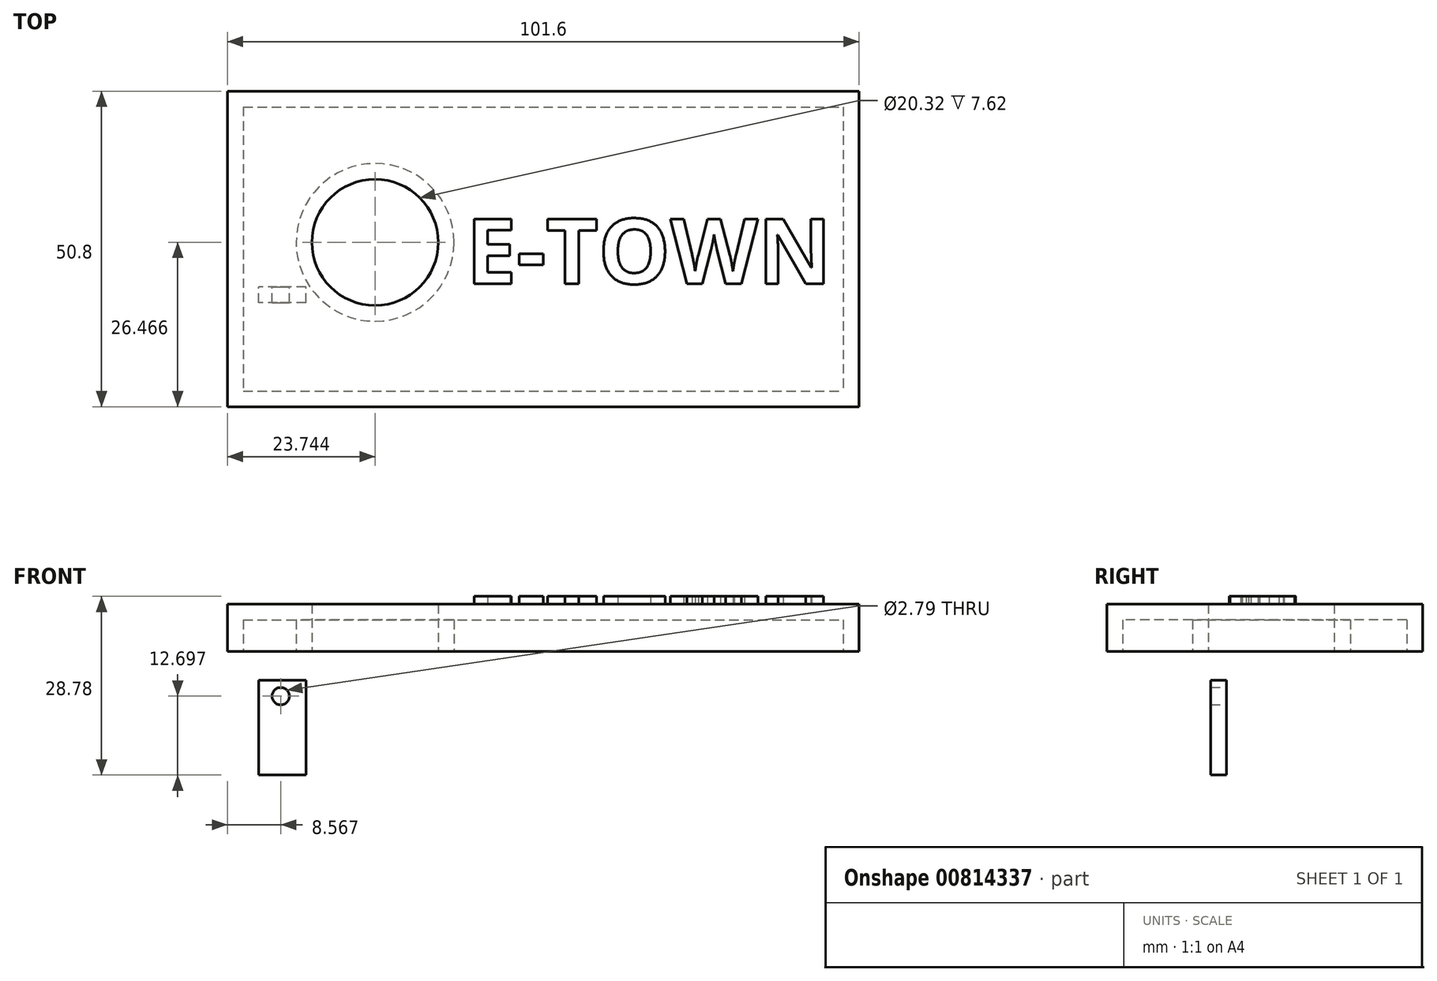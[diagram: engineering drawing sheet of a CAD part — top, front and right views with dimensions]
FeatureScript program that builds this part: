
annotation { "Feature Type Name" : "Feature", "Feature Type Description" : "" }
export const myFeature = defineFeature(function(context is Context, id is Id, definition is map)
    precondition{}
    {
        {
            var Q0;
            Q0=qCreatedBy(makeId("Top.planeOp"),FACE);
            var sketch = newSketch(context, id + "F0", { "sketchPlane" : qUnion([Q0])});
            skLineSegment(sketch, "E0.bottom", {"start": v(-46.2, 31.5) * mm, "end": v(55.4, 31.5) * mm});
            skLineSegment(sketch, "E0.top", {"start": v(-46.2, -19.3) * mm, "end": v(55.4, -19.3) * mm});
            skLineSegment(sketch, "E0.left", {"start": v(-46.2, 31.5) * mm, "end": v(-46.2, -19.3) * mm});
            skLineSegment(sketch, "E0.right", {"start": v(55.4, 31.5) * mm, "end": v(55.4, -19.3) * mm});
            skCircle(sketch, "E1", {"center": v(-22.45, 7.18) * mm, "radius": 10.16 * mm});
            skSolve(sketch);
        }
        {
            var Q0;
            Q0=makeQuery(id+"F0.imprint","IMPRINT",FACE,{"disambiguationData":[TD([[makeQuery(id+"F0.imprint","IMPRINT",EDGE,{"derivedFrom":sQuery(id+"F0.wireOp",EDGE,"E0.bottom")}),-1.0]])]});
            extrude(context, id + "F1", {"entities" : qUnion([Q0]), "depth" : 7.62 * mm, "offsetDistance" : 25.4 * mm});
        }
        {
            var Q0;
            Q0=makeQuery(id+"F1.opExtrude","CAP_FACE",FACE,{"disambiguationData":[OSD([sQuery(id+"F0.wireOp",EDGE,"E0.bottom"),sQuery(id+"F0.wireOp",EDGE,"E0.top"),sQuery(id+"F0.wireOp",EDGE,"E0.left"),sQuery(id+"F0.wireOp",EDGE,"E0.right")])],"isStart":true});
            shell(context, id + "F2", {"entities" : qUnion([Q0]), "thickness" : 2.54 * mm});
        }
        {
            var Q0;
            Q0=qCreatedBy(makeId("Front.planeOp"),FACE);
            var sketch = newSketch(context, id + "F3", { "sketchPlane" : qUnion([Q0])});
            skLineSegment(sketch, "E2.bottom", {"start": v(-33.58, -4.65) * mm, "end": v(-41.2, -4.65) * mm});
            skLineSegment(sketch, "E2.top", {"start": v(-33.58, -19.9) * mm, "end": v(-41.2, -19.9) * mm});
            skLineSegment(sketch, "E2.left", {"start": v(-33.58, -4.65) * mm, "end": v(-33.58, -19.9) * mm});
            skLineSegment(sketch, "E2.right", {"start": v(-41.2, -4.65) * mm, "end": v(-41.2, -19.9) * mm});
            skCircle(sketch, "E3", {"center": v(-37.62, -7.2) * mm, "radius": 1.4 * mm});
            skSolve(sketch);
        }
        {
            var Q0;
            Q0=makeQuery(id+"F3.imprint","IMPRINT",FACE,{"disambiguationData":[TD([[makeQuery(id+"F3.imprint","IMPRINT",EDGE,{"derivedFrom":sQuery(id+"F3.wireOp",EDGE,"E2.bottom")}),1.0]])]});
            extrude(context, id + "F4", {"entities" : qUnion([Q0]), "depth" : 2.54 * mm, "offsetDistance" : 25.4 * mm});
        }
        {
            var Q0;
            Q0=makeQuery(id+"F1.opExtrude","CAP_FACE",FACE,{"disambiguationData":[OSD([sQuery(id+"F0.wireOp",EDGE,"E0.bottom"),sQuery(id+"F0.wireOp",EDGE,"E0.top"),sQuery(id+"F0.wireOp",EDGE,"E0.left"),sQuery(id+"F0.wireOp",EDGE,"E0.right"),sQuery(id+"F0.wireOp",EDGE,"E1")])],"isStart":false});
            var sketch = newSketch(context, id + "F5", { "sketchPlane" : qUnion([Q0])});
            skText(sketch, "E4", { "text": "E-TOWN", "fontName": "OpenSans-Bold.ttf"});
            const initialGuessF5  = {"E4": [-0.00783, 0.00053, 1, 0, 0.01049]};
            skSetInitialGuess(sketch, initialGuessF5);
            skSolve(sketch);
        }
        {
            var Q0;
            Q0 = qSketchRegion(id + "F5", true);
            extrude(context, id + "F6", {"entities" : qUnion([Q0]), "operationType" : NewBodyOperationType.ADD, "depth" : 1.27 * mm, "offsetDistance" : 25.4 * mm});
        }
    });
